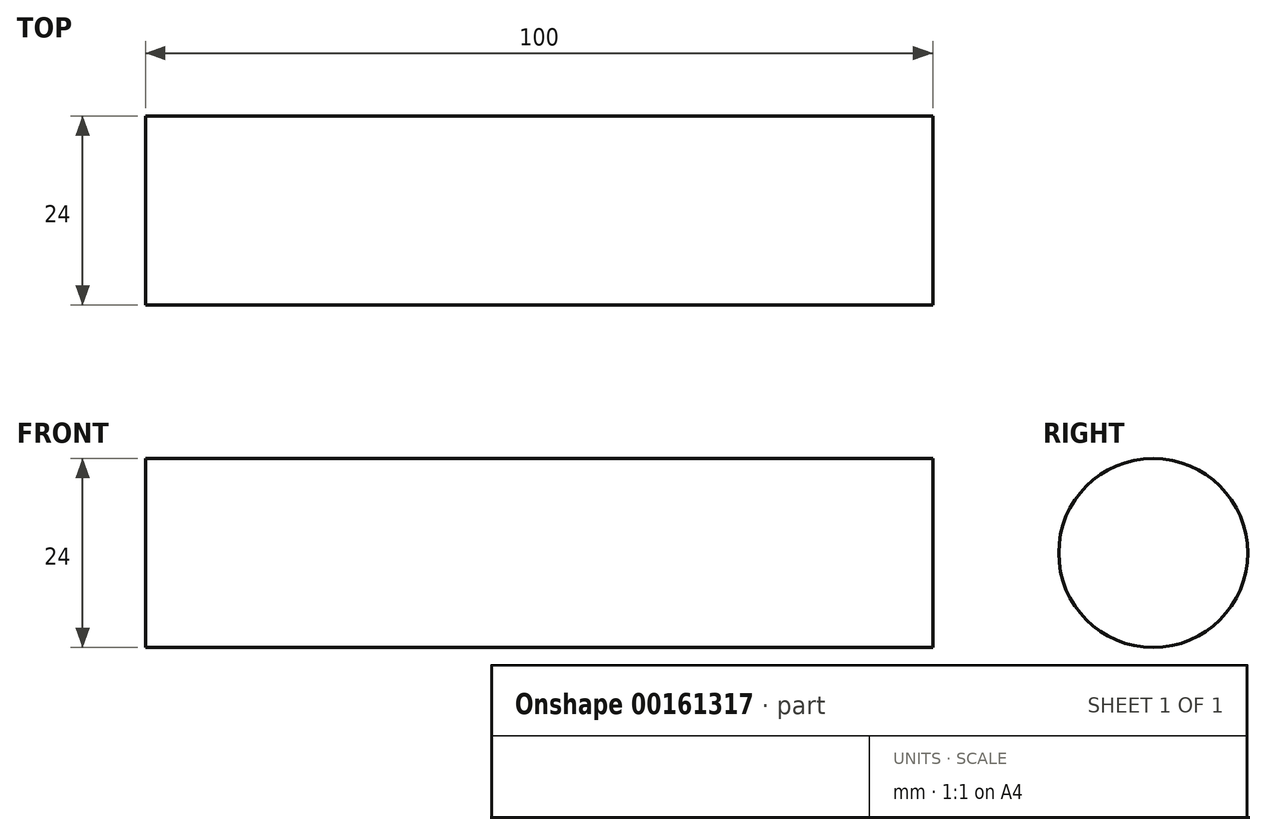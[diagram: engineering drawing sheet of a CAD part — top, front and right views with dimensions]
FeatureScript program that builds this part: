
annotation { "Feature Type Name" : "Feature", "Feature Type Description" : "" }
export const myFeature = defineFeature(function(context is Context, id is Id, definition is map)
    precondition{}
    {
        {
            var Q0;
            Q0=qCreatedBy(makeId("Right.planeOp"),FACE);
            var sketch = newSketch(context, id + "F0", { "sketchPlane" : qUnion([Q0])});
            skCircle(sketch, "E0", {"center": v(0, 0) * mm, "radius": 12 * mm});
            skSolve(sketch);
        }
        {
            var Q0;
            Q0 = qSketchRegion(id + "F0", true);
            extrude(context, id + "F1", {"entities" : qUnion([Q0]), "endBound" : BoundingType.SYMMETRIC, "depth" : 100 * mm});
        }
    });
